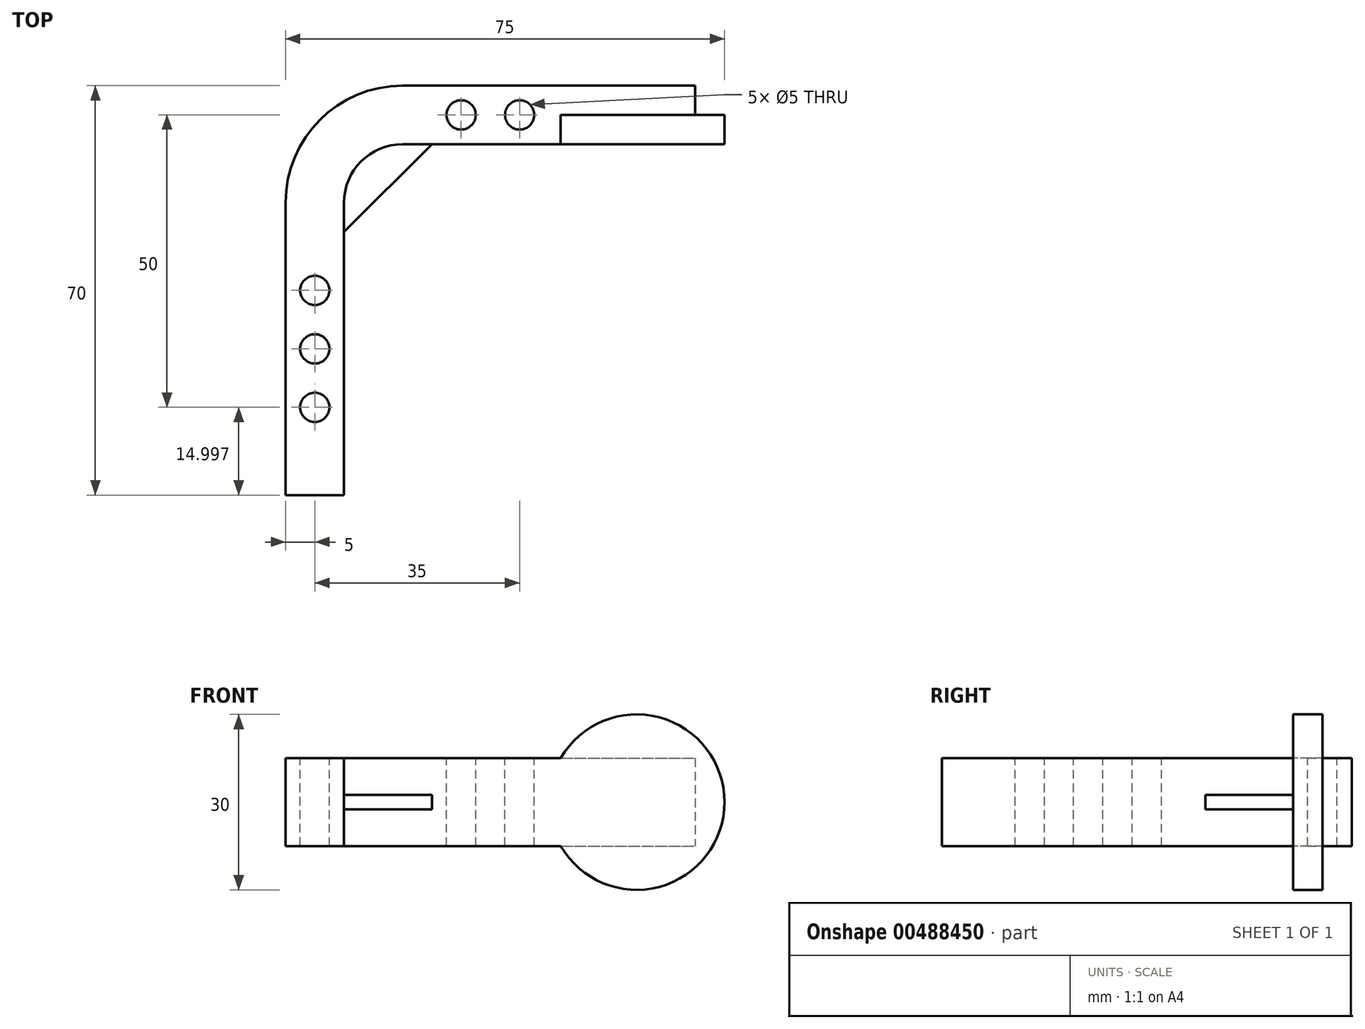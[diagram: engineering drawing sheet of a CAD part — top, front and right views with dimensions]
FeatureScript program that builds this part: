
annotation { "Feature Type Name" : "Feature", "Feature Type Description" : "" }
export const myFeature = defineFeature(function(context is Context, id is Id, definition is map)
    precondition{}
    {
        {
            var Q0;
            Q0=qCreatedBy(makeId("Top.planeOp"),FACE);
            var sketch = newSketch(context, id + "F0", { "sketchPlane" : qUnion([Q0])});
            skLineSegment(sketch, "E0", {"start": v(0, 21.3) * mm, "end": v(0, -28.7) * mm});
            skLineSegment(sketch, "E1", {"start": v(20, 41.3) * mm, "end": v(70, 41.3) * mm});
            skPoint(sketch, "E2.visualSharp", {"position": v(0, 41.3) * mm});
            skArc(sketch, "E2.filletArc", {"start": v(20, 41.3) * mm, "mid": v(5.86, 35.45) * mm, "end": v(0, 21.3) * mm});
            skLineSegment(sketch, "E3", {"start": v(0, -28.7) * mm, "end": v(10, -28.7) * mm});
            skLineSegment(sketch, "E4", {"start": v(10, -28.7) * mm, "end": v(10, 21.3) * mm});
            skLineSegment(sketch, "E5", {"start": v(20, 31.3) * mm, "end": v(70, 31.3) * mm});
            skLineSegment(sketch, "E6", {"start": v(70, 41.3) * mm, "end": v(70, 31.3) * mm});
            skPoint(sketch, "E7.newPointA", {"position": v(10, 21.3) * mm});
            skPoint(sketch, "E7.newPointB", {"position": v(20, 31.3) * mm});
            skArc(sketch, "E7.filletArc", {"start": v(20, 31.3) * mm, "mid": v(12.93, 28.38) * mm, "end": v(10, 21.3) * mm});
            skSolve(sketch);
        }
        {
            var Q0;
            Q0=makeQuery(id+"F0.imprint","IMPRINT",FACE,{"disambiguationData":[TD([[makeQuery(id+"F0.imprint","IMPRINT",EDGE,{"derivedFrom":sQuery(id+"F0.wireOp",EDGE,"E0")}),1.0]])]});
            extrude(context, id + "F1", {"entities" : qUnion([Q0]), "depth" : 15 * mm});
        }
        {
            var Q0;
            Q0=makeQuery(id+"F1.opExtrude","CAP_FACE",FACE,{"disambiguationData":[OSD([sQuery(id+"F0.wireOp",EDGE,"E0"),sQuery(id+"F0.wireOp",EDGE,"E1"),sQuery(id+"F0.wireOp",EDGE,"E2.filletArc"),sQuery(id+"F0.wireOp",EDGE,"E3"),sQuery(id+"F0.wireOp",EDGE,"E4"),sQuery(id+"F0.wireOp",EDGE,"E5"),sQuery(id+"F0.wireOp",EDGE,"E6"),sQuery(id+"F0.wireOp",EDGE,"E7.filletArc")])],"isStart":false});
            cPlane(context, id + "F2", {"entities" : qUnion([Q0]), "cplaneType" : CPlaneType.OFFSET, "offset" : 7.5 * mm, "oppositeDirection" : true, "width" : 150 * mm, "height" : 150 * mm});
        }
        {
            var Q0;
            Q0=qCreatedBy(id+"F2.planeOp",FACE);
            var sketch = newSketch(context, id + "F3", { "sketchPlane" : qUnion([Q0])});
            skLineSegment(sketch, "E8", {"start": v(10, 16.3) * mm, "end": v(25, 31.3) * mm});
            skLineSegment(sketch, "E9", {"start": v(10, 16.3) * mm, "end": v(10, 31.3) * mm});
            skLineSegment(sketch, "E10", {"start": v(10, 31.3) * mm, "end": v(25, 31.3) * mm});
            skSolve(sketch);
        }
        {
            var Q0;
            Q0=makeQuery(id+"F3.imprint","IMPRINT",FACE,{"disambiguationData":[TD([[makeQuery(id+"F3.imprint","IMPRINT",EDGE,{"derivedFrom":sQuery(id+"F3.wireOp",EDGE,"E8")}),1.0]])]});
            extrude(context, id + "F4", {"entities" : qUnion([Q0]), "operationType" : NewBodyOperationType.ADD, "endBound" : BoundingType.SYMMETRIC, "depth" : 2.5 * mm});
        }
        {
            var Q0;
            Q0=makeQuery(id+"F1.opExtrude","CAP_FACE",FACE,{"disambiguationData":[OSD([sQuery(id+"F0.wireOp",EDGE,"E0"),sQuery(id+"F0.wireOp",EDGE,"E1"),sQuery(id+"F0.wireOp",EDGE,"E2.filletArc"),sQuery(id+"F0.wireOp",EDGE,"E3"),sQuery(id+"F0.wireOp",EDGE,"E4"),sQuery(id+"F0.wireOp",EDGE,"E5"),sQuery(id+"F0.wireOp",EDGE,"E6"),sQuery(id+"F0.wireOp",EDGE,"E7.filletArc")])],"isStart":false});
            var sketch = newSketch(context, id + "F5", { "sketchPlane" : qUnion([Q0])});
            skCircle(sketch, "E11", {"center": v(5, -13.7) * mm, "radius": 2.5 * mm});
            skCircle(sketch, "E12", {"center": v(5, -3.7) * mm, "radius": 2.5 * mm});
            skCircle(sketch, "E13", {"center": v(5, 6.3) * mm, "radius": 2.5 * mm});
            skCircle(sketch, "E14", {"center": v(30, 36.3) * mm, "radius": 2.5 * mm});
            skCircle(sketch, "E15", {"center": v(40, 36.3) * mm, "radius": 2.5 * mm});
            skSolve(sketch);
        }
        {
            var Q0;
            Q0 = qSketchRegion(id + "F5", true);
            extrude(context, id + "F6", {"entities" : qUnion([Q0]), "operationType" : NewBodyOperationType.REMOVE, "endBound" : BoundingType.UP_TO_NEXT, "oppositeDirection" : true, "depth" : 25 * mm});
        }
        {
            var Q0;
            Q0=makeQuery(id+"F1.opExtrude","SWEPT_FACE",FACE,{"disambiguationData":[OSD([sQuery(id+"F0.wireOp",EDGE,"E5")])]});
            var sketch = newSketch(context, id + "F7", { "sketchPlane" : qUnion([Q0])});
            skCircle(sketch, "E16", {"center": v(60, 7.5) * mm, "radius": 15 * mm});
            skSolve(sketch);
        }
        {
            var Q0;
            {var subQ1=sQuery(id+"F0.wireOp",EDGE,"E5");var subQ6=makeQuery(id+"F1.opExtrude","SWEPT_EDGE",EDGE,{"disambiguationData":[OSD([subQ1,sQuery(id+"F0.wireOp",EDGE,"E6")])]});Q0=makeQuery(id+"F7.imprint","IMPRINT",FACE,{"disambiguationData":[TD([[makeQuery(id+"F7.imprint","IMPRINT",EDGE,{"derivedFrom":subQ6}),1.0]])]});}
            var Q1;
            {var subQ1=sQuery(id+"F0.wireOp",EDGE,"E5");var subQ6=makeQuery(id+"F1.opExtrude","SWEPT_EDGE",EDGE,{"disambiguationData":[OSD([subQ1,sQuery(id+"F0.wireOp",EDGE,"E6")])]});Q1=makeQuery(id+"F7.imprint","IMPRINT",FACE,{"disambiguationData":[TD([[makeQuery(id+"F7.imprint","IMPRINT",EDGE,{"derivedFrom":subQ6}),-1.0]])]});}
            extrude(context, id + "F8", {"entities" : qUnion([Q0, Q1]), "operationType" : NewBodyOperationType.ADD, "oppositeDirection" : true, "depth" : 5 * mm});
        }
    });
